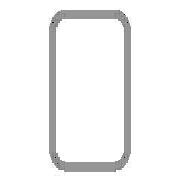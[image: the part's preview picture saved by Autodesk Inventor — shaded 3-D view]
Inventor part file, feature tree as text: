
AUTODESK INVENTOR PART (.ipt)
format: ipt  version: 2025 (Build 290162010, 162A)  size: 141,824 bytes
history: native  units: mm (DEFAULTED — no unit token found)
features: other x4, plane x2, split x1, sketch x1
ambient origin geometry x8: Origin, YZ Plane, XZ Plane, XY Plane, X Axis, Y Axis, Z Axis, Center Point
bodies: Solid1 (feature_tree), Body (feature_tree)
feature tree (8):
  parser-record x1  (decoder bookkeeping rows leaked as tree rows — omitted from the tree; the rows remain in map.json)
  other  "Driven Length"
  other  "Start Plane"
  other  "End Plane"
  plane  "Work Plane4"
  split  "Split1"
  sketch  "Sketch3"  dims[d3=809.237711mm d4=0.0mm d7=4.0mm d9=20.0mm d11=40.0mm d12=2.0mm d13=-0.0mm d14=809.237711mm d15=10.0mm d16=20.0mm d17=90.0deg d18=809.237711mm]
  plane  "Work Plane3"
